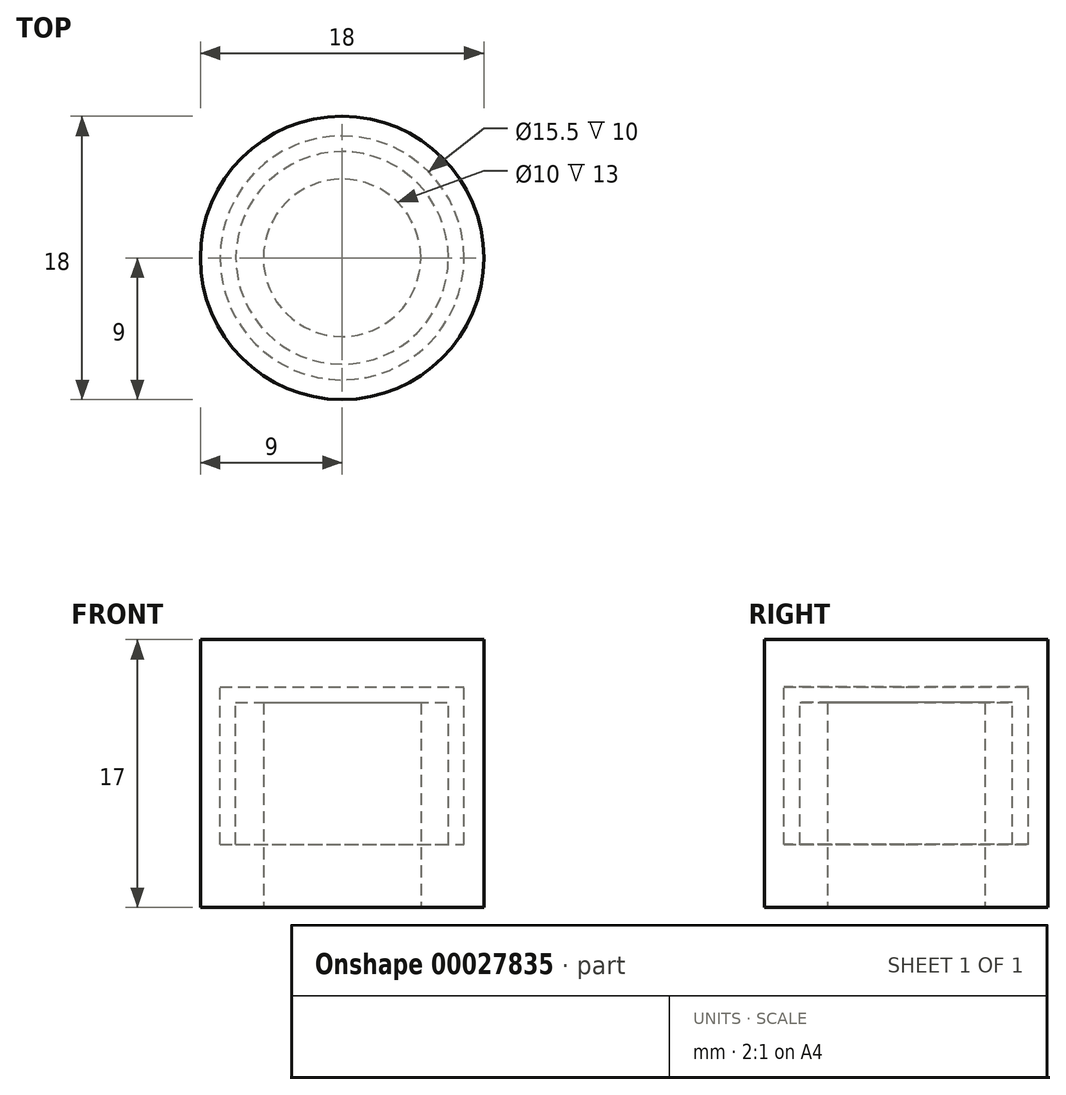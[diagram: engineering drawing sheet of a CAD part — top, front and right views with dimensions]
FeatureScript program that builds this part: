
annotation { "Feature Type Name" : "Feature", "Feature Type Description" : "" }
export const myFeature = defineFeature(function(context is Context, id is Id, definition is map)
    precondition{}
    {
        {
            var Q0;
            Q0=qCreatedBy(makeId("Top.planeOp"),FACE);
            var sketch = newSketch(context, id + "F0", { "sketchPlane" : qUnion([Q0])});
            skCircle(sketch, "E0", {"center": v(0, 0) * mm, "radius": 9 * mm});
            skSolve(sketch);
        }
        {
            var Q0;
            Q0=makeQuery(id+"F0.imprint","IMPRINT",FACE,{"disambiguationData":[TD([[makeQuery(id+"F0.imprint","IMPRINT",EDGE,{"derivedFrom":sQuery(id+"F0.wireOp",EDGE,"E0")}),1.0]])]});
            extrude(context, id + "F1", {"entities" : qUnion([Q0]), "depth" : 17 * mm});
        }
        {
            var Q0;
            Q0=makeQuery(id+"F1.opExtrude","CAP_FACE",FACE,{"disambiguationData":[OSD([sQuery(id+"F0.wireOp",EDGE,"E0")])],"isStart":true});
            var sketch = newSketch(context, id + "F2", { "sketchPlane" : qUnion([Q0])});
            skCircle(sketch, "E1", {"center": v(0, 0) * mm, "radius": 5 * mm});
            skSolve(sketch);
        }
        {
            var Q0;
            Q0=makeQuery(id+"F2.imprint","IMPRINT",FACE,{"disambiguationData":[TD([[makeQuery(id+"F2.imprint","IMPRINT",EDGE,{"derivedFrom":sQuery(id+"F2.wireOp",EDGE,"E1")}),1.0]])]});
            extrude(context, id + "F3", {"entities" : qUnion([Q0]), "operationType" : NewBodyOperationType.REMOVE, "oppositeDirection" : true, "depth" : 14 * mm});
        }
        {
            var Q0;
            Q0=makeQuery(id+"F3.boolean.opBoolean","COPY",FACE,{"derivedFrom":makeQuery(id+"F3.opExtrude","CAP_FACE",FACE,{"disambiguationData":[OSD([sQuery(id+"F2.wireOp",EDGE,"E1")])],"isStart":false})});
            var sketch = newSketch(context, id + "F4", { "sketchPlane" : qUnion([Q0])});
            skCircle(sketch, "E2", {"center": v(0, 0) * mm, "radius": 6.75 * mm});
            skCircle(sketch, "E3", {"center": v(0, 0) * mm, "radius": 7.75 * mm});
            skSolve(sketch);
        }
        {
            var Q0;
            Q0=makeQuery(id+"F4.imprint","IMPRINT",FACE,{"disambiguationData":[TD([[makeQuery(id+"F4.imprint","IMPRINT",EDGE,{"derivedFrom":sQuery(id+"F4.wireOp",EDGE,"E2")}),-1.0]])]});
            extrude(context, id + "F5", {"entities" : qUnion([Q0]), "operationType" : NewBodyOperationType.REMOVE, "depth" : 10 * mm});
        }
        {
            var Q0;
            Q0=makeQuery(id+"F4.imprint","IMPRINT",FACE,{"disambiguationData":[TD([[makeQuery(id+"F4.imprint","IMPRINT",EDGE,{"derivedFrom":sQuery(id+"F4.wireOp",EDGE,"E2")}),1.0]])]});
            extrude(context, id + "F6", {"entities" : qUnion([Q0]), "operationType" : NewBodyOperationType.REMOVE, "depth" : 1 * mm});
        }
    });
